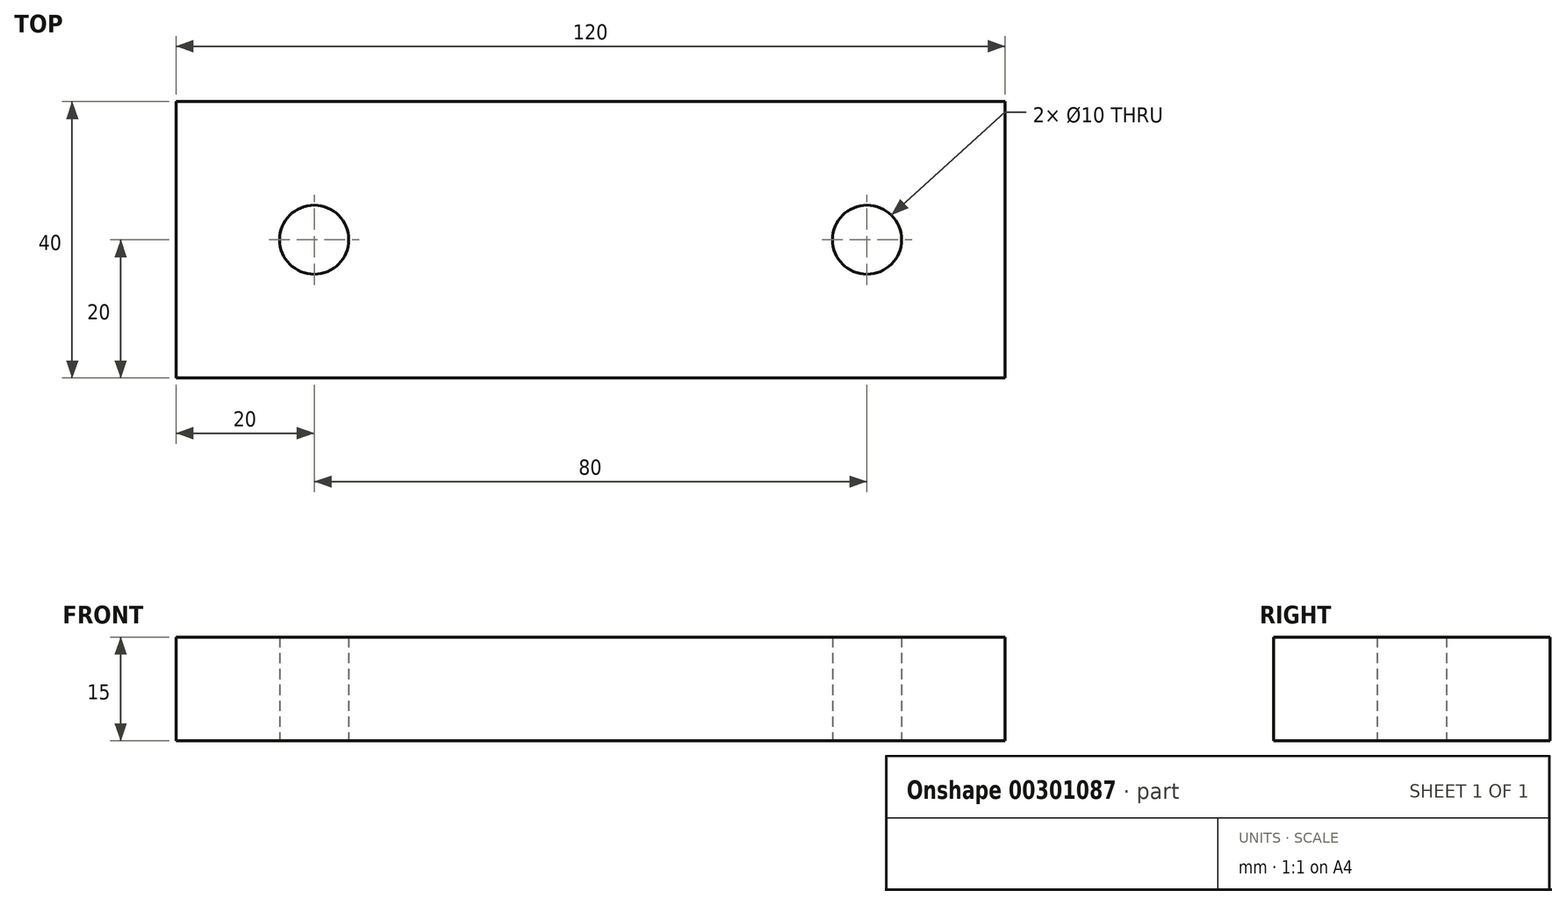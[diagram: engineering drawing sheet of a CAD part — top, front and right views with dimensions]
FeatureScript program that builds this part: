
annotation { "Feature Type Name" : "Feature", "Feature Type Description" : "" }
export const myFeature = defineFeature(function(context is Context, id is Id, definition is map)
    precondition{}
    {
        {
            var Q0;
            Q0=qCreatedBy(makeId("Top.planeOp"),FACE);
            var sketch = newSketch(context, id + "F0", { "sketchPlane" : qUnion([Q0])});
            skLineSegment(sketch, "E0.bottom", {"start": v(0, 0) * mm, "end": v(120, 0) * mm});
            skLineSegment(sketch, "E0.top", {"start": v(0, -40) * mm, "end": v(120, -40) * mm});
            skLineSegment(sketch, "E0.left", {"start": v(0, 0) * mm, "end": v(0, -40) * mm});
            skLineSegment(sketch, "E0.right", {"start": v(120, 0) * mm, "end": v(120, -40) * mm});
            skCircle(sketch, "E1", {"center": v(20, -20) * mm, "radius": 5 * mm});
            skCircle(sketch, "E2", {"center": v(100, -20) * mm, "radius": 5 * mm});
            skSolve(sketch);
        }
        {
            var Q0;
            Q0 = qSketchRegion(id + "F0", true);
            extrude(context, id + "F1", {"entities" : qUnion([Q0]), "depth" : 15 * mm});
        }
    });
